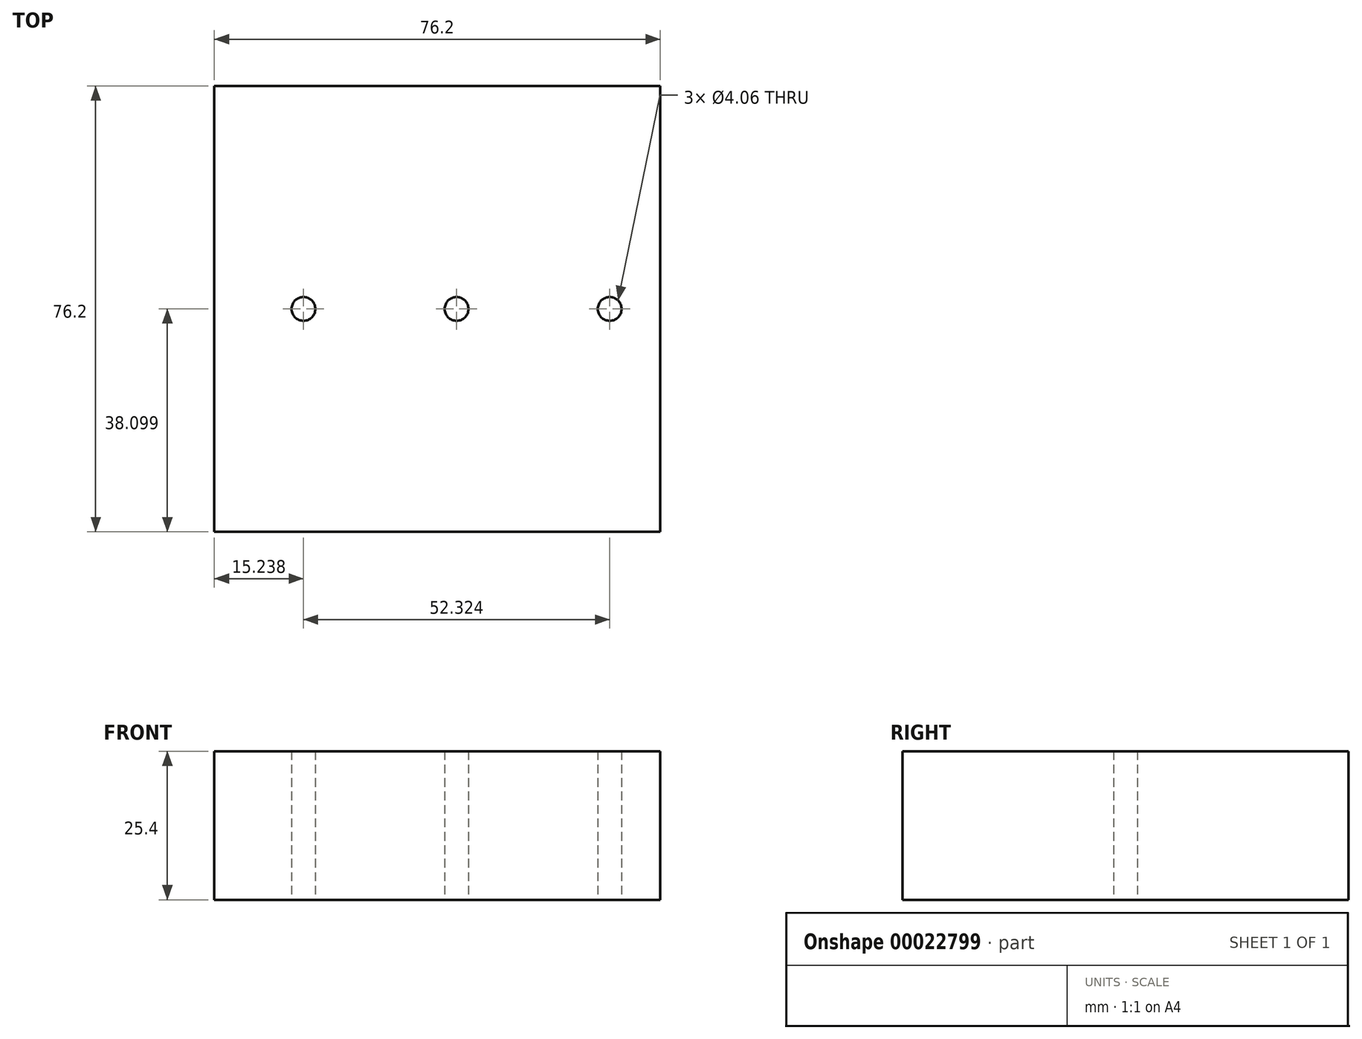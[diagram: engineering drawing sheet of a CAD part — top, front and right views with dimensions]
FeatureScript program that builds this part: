
annotation { "Feature Type Name" : "Feature", "Feature Type Description" : "" }
export const myFeature = defineFeature(function(context is Context, id is Id, definition is map)
    precondition{}
    {
        {
            var Q0;
            Q0=qCreatedBy(makeId("Top.planeOp"),FACE);
            var sketch = newSketch(context, id + "F0", { "sketchPlane" : qUnion([Q0])});
            skLineSegment(sketch, "E0.bottom", {"start": v(12.79, 63.67) * mm, "end": v(88.99, 63.67) * mm});
            skLineSegment(sketch, "E0.top", {"start": v(12.79, -12.53) * mm, "end": v(88.99, -12.53) * mm});
            skLineSegment(sketch, "E0.left", {"start": v(12.79, 63.67) * mm, "end": v(12.79, -12.53) * mm});
            skLineSegment(sketch, "E0.right", {"start": v(88.99, 63.67) * mm, "end": v(88.99, -12.53) * mm});
            skCircle(sketch, "E1", {"center": v(28.03, 25.57) * mm, "radius": 2.03 * mm});
            skLineSegment(sketch, "E2", {"start": v(28.03, 25.57) * mm, "end": v(30.06, 25.57) * mm});
            skCircle(sketch, "E3", {"center": v(54.19, 25.57) * mm, "radius": 2.03 * mm});
            skLineSegment(sketch, "E4", {"start": v(54.19, 25.57) * mm, "end": v(52.16, 25.57) * mm});
            skCircle(sketch, "E5", {"center": v(80.35, 25.57) * mm, "radius": 2.03 * mm});
            skLineSegment(sketch, "E6", {"start": v(80.35, 25.57) * mm, "end": v(80.35, 23.54) * mm});
            skLineSegment(sketch, "E7", {"start": v(28.03, 25.57) * mm, "end": v(28.03, 23.54) * mm});
            skLineSegment(sketch, "E8", {"start": v(54.19, 25.57) * mm, "end": v(54.19, 23.54) * mm});
            skLineSegment(sketch, "E9", {"start": v(12.79, -12.53) * mm, "end": v(28.03, -12.53) * mm});
            skLineSegment(sketch, "E10", {"start": v(54.19, -12.53) * mm, "end": v(12.79, -12.53) * mm});
            skPoint(sketch, "E11.orphan", {"position": v(12.79, 25.57) * mm});
            skLineSegment(sketch, "E12.trimOffspring", {"start": v(82.38, 25.57) * mm, "end": v(78.32, 25.57) * mm});
            skLineSegment(sketch, "E13.trimOffspring", {"start": v(30.06, 25.57) * mm, "end": v(26, 25.57) * mm});
            skLineSegment(sketch, "E14", {"start": v(80.35, 25.57) * mm, "end": v(78.32, 25.57) * mm});
            skLineSegment(sketch, "E15.trimOffspring", {"start": v(56.22, 25.57) * mm, "end": v(52.16, 25.57) * mm});
            skLineSegment(sketch, "E16", {"start": v(30.06, 25.57) * mm, "end": v(52.16, 25.57) * mm});
            skLineSegment(sketch, "E17", {"start": v(56.22, 25.57) * mm, "end": v(78.32, 25.57) * mm});
            skSolve(sketch);
        }
        {
            var Q0;
            Q0=makeQuery(id+"F0.imprint","IMPRINT",FACE,{"disambiguationData":[TD([[makeQuery(id+"F0.imprint","IMPRINT",EDGE,{"derivedFrom":sQuery(id+"F0.wireOp",EDGE,"E0.bottom")}),-1.0]])]});
            extrude(context, id + "F1", {"entities" : qUnion([Q0]), "depth" : 25.4 * mm});
        }
    });
